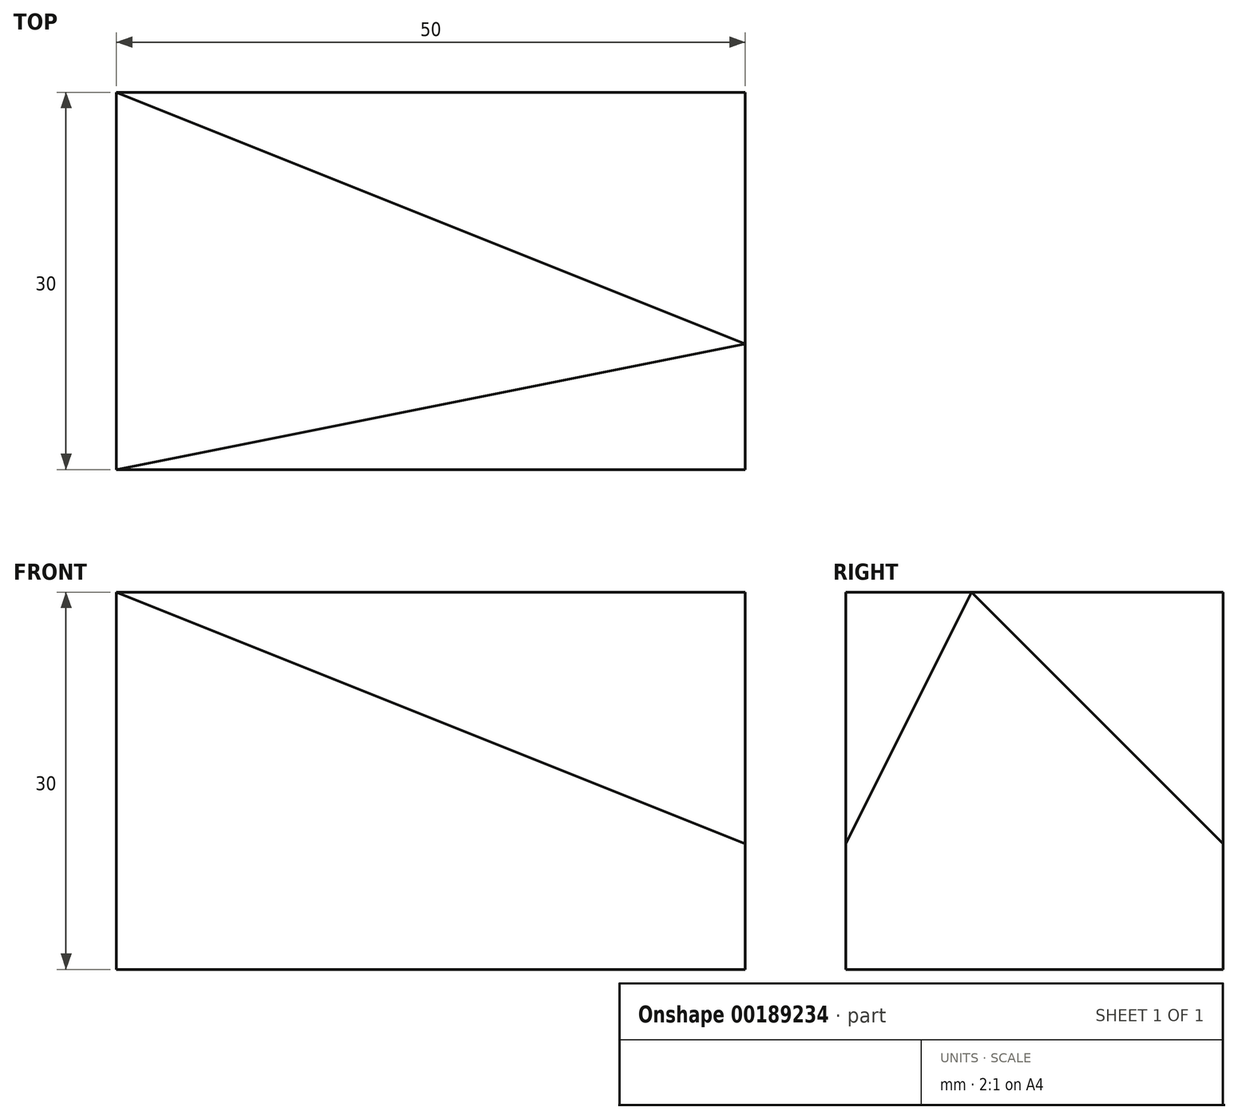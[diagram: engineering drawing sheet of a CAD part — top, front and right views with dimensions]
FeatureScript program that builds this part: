
annotation { "Feature Type Name" : "Feature", "Feature Type Description" : "" }
export const myFeature = defineFeature(function(context is Context, id is Id, definition is map)
    precondition{}
    {
        {
            var Q0;
            Q0=qCreatedBy(makeId("Top.planeOp"),FACE);
            var sketch = newSketch(context, id + "F0", { "sketchPlane" : qUnion([Q0])});
            skLineSegment(sketch, "E0.bottom", {"start": v(0, 0) * mm, "end": v(50, 0) * mm});
            skLineSegment(sketch, "E0.top", {"start": v(0, 30) * mm, "end": v(50, 30) * mm});
            skLineSegment(sketch, "E0.left", {"start": v(0, 0) * mm, "end": v(0, 30) * mm});
            skLineSegment(sketch, "E0.right", {"start": v(50, 0) * mm, "end": v(50, 30) * mm});
            skSolve(sketch);
        }
        {
            var Q0;
            Q0=makeQuery(id+"F0.imprint","IMPRINT",FACE,{"disambiguationData":[TD([[makeQuery(id+"F0.imprint","IMPRINT",EDGE,{"derivedFrom":sQuery(id+"F0.wireOp",EDGE,"E0.bottom")}),1.0]])]});
            extrude(context, id + "F1", {"entities" : qUnion([Q0]), "depth" : 30 * mm});
        }
        {
            var Q0;
            Q0=makeQuery(id+"F1.opExtrude","SWEPT_FACE",FACE,{"disambiguationData":[OSD([sQuery(id+"F0.wireOp",EDGE,"E0.right")])]});
            var sketch = newSketch(context, id + "F2", { "sketchPlane" : qUnion([Q0])});
            skPoint(sketch, "E1", {"position": v(10, 30) * mm});
            skPoint(sketch, "E2", {"position": v(0, 10) * mm});
            skPoint(sketch, "E3", {"position": v(30, 10) * mm});
            skSolve(sketch);
        }
        {
            var Q0;
            Q0=makeQuery(id+"F1.opExtrude","CAP_VERTEX",VERTEX,{"disambiguationData":[OSD([sQuery(id+"F0.wireOp",EDGE,"E0.bottom"),sQuery(id+"F0.wireOp",EDGE,"E0.left")])],"isStart":false});
            var Q1;
            Q1=sQuery(id+"F2.wireOp",VERTEX,"E1");
            var Q2;
            Q2=sQuery(id+"F2.wireOp",VERTEX,"E2");
            cPlane(context, id + "F3", {"entities" : qUnion([Q0, Q1, Q2]), "cplaneType" : CPlaneType.THREE_POINT, "offset" : 25 * mm, "width" : 150 * mm, "height" : 150 * mm});
        }
        {
            var Q0;
            Q0=makeQuery(id+"F1.opExtrude","CAP_VERTEX",VERTEX,{"disambiguationData":[OSD([sQuery(id+"F0.wireOp",EDGE,"E0.top"),sQuery(id+"F0.wireOp",EDGE,"E0.left")])],"isStart":false});
            var Q1;
            Q1=sQuery(id+"F2.wireOp",VERTEX,"E3");
            var Q2;
            Q2=sQuery(id+"F2.wireOp",VERTEX,"E1");
            cPlane(context, id + "F4", {"entities" : qUnion([Q0, Q1, Q2]), "cplaneType" : CPlaneType.THREE_POINT, "offset" : 25 * mm, "width" : 150 * mm, "height" : 150 * mm});
        }
        {
            var Q0;
            Q0=qCreatedBy(id+"F3.planeOp",FACE);
            var sketch = newSketch(context, id + "F5", { "sketchPlane" : qUnion([Q0])});
            skLineSegment(sketch, "E4", {"start": v(48.43, 31.3) * mm, "end": v(-2.36, 26.83) * mm});
            skLineSegment(sketch, "E5", {"start": v(-2.36, 26.83) * mm, "end": v(48.43, 8.94) * mm});
            skLineSegment(sketch, "E6", {"start": v(48.43, 8.94) * mm, "end": v(48.43, 31.3) * mm});
            skSolve(sketch);
        }
        {
            var Q0;
            Q0=makeQuery(id+"F5.imprint","IMPRINT",FACE,{"disambiguationData":[TD([[makeQuery(id+"F5.imprint","IMPRINT",EDGE,{"derivedFrom":sQuery(id+"F5.wireOp",EDGE,"E4")}),1.0]])]});
            extrude(context, id + "F6", {"entities" : qUnion([Q0]), "operationType" : NewBodyOperationType.REMOVE, "endBound" : BoundingType.THROUGH_ALL, "depth" : 25 * mm});
        }
        {
            var Q0;
            Q0=qCreatedBy(id+"F4.planeOp",FACE);
            var sketch = newSketch(context, id + "F7", { "sketchPlane" : qUnion([Q0])});
            skLineSegment(sketch, "E7", {"start": v(11.55, 0) * mm, "end": v(-40.41, 14.14) * mm});
            skLineSegment(sketch, "E8", {"start": v(-40.41, 14.14) * mm, "end": v(-40.41, -14.14) * mm});
            skLineSegment(sketch, "E9", {"start": v(-40.41, -14.14) * mm, "end": v(11.55, 0) * mm});
            skSolve(sketch);
        }
        {
            var Q0;
            Q0=makeQuery(id+"F7.imprint","IMPRINT",FACE,{"disambiguationData":[TD([[makeQuery(id+"F7.imprint","IMPRINT",EDGE,{"derivedFrom":sQuery(id+"F7.wireOp",EDGE,"E7")}),1.0]])]});
            extrude(context, id + "F8", {"entities" : qUnion([Q0]), "operationType" : NewBodyOperationType.REMOVE, "endBound" : BoundingType.THROUGH_ALL, "depth" : 25 * mm});
        }
    });
